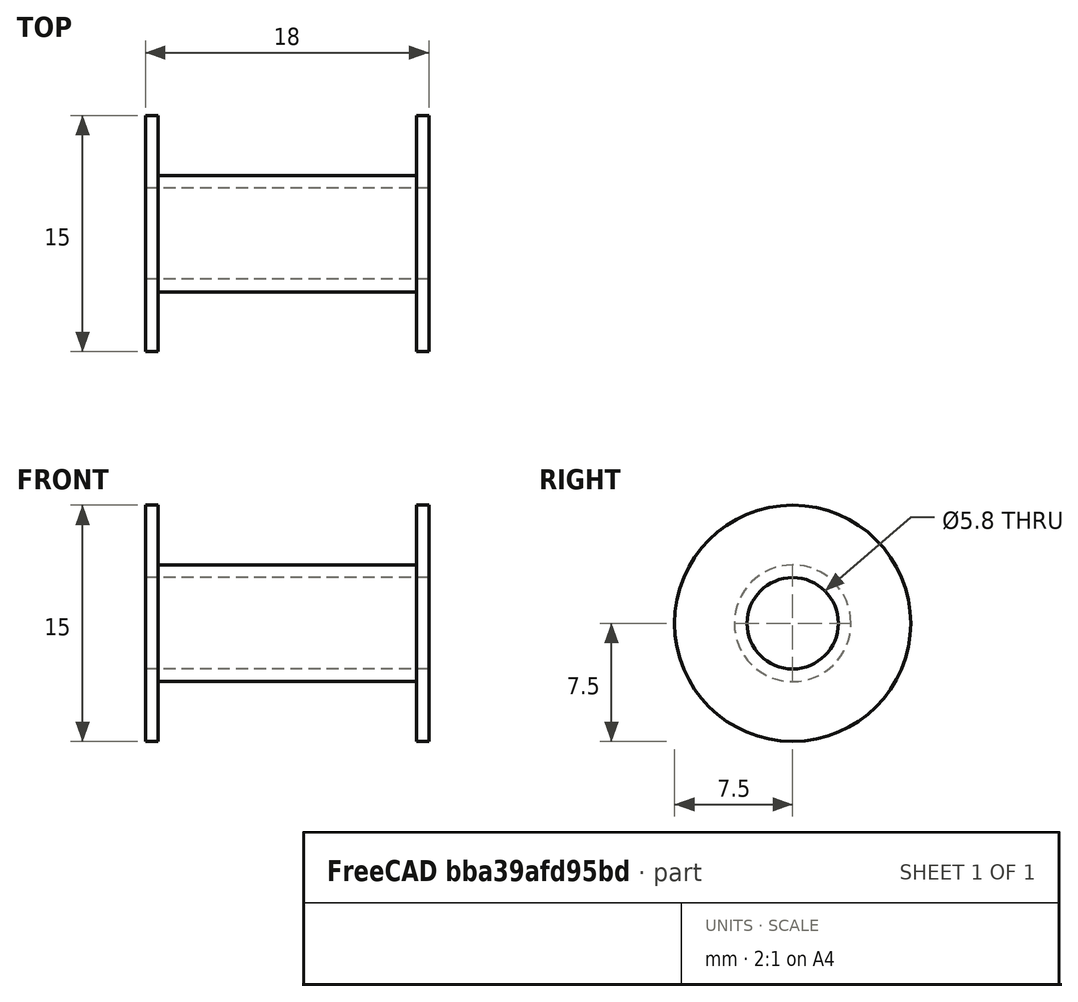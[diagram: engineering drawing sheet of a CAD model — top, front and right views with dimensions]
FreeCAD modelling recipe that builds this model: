
FCSTD DOCUMENT  (FreeCAD 0.17R13541 (Git))
Label: coil-core
License: All rights reserved
LicenseURL: http://en.wikipedia.org/wiki/All_rights_reserved
objects: Sketcher::SketchObject×1, PartDesign::Revolution×1, PartDesign::Body×1
note: 4 computed .brp shape members not serialized (recipe doc carries the construction recipe); baked Part::Feature solids carry a one-line shape summary decoded from their .brp

FEATURE [Sketcher::SketchObject] Sketch
  MapMode = 5
  Placement = pos=(0,0,0) rot=(1,0,0;1.5708rad)
  Support = -> [XZ_Plane]
  sketch-geometry (8):
    g0: LineSegment StartX=-9 StartY=-2.9 StartZ=0 EndX=-9 EndY=-7.5 EndZ=0
    g1: LineSegment StartX=-9 StartY=-7.5 StartZ=0 EndX=-8.2 EndY=-7.5 EndZ=0
    g2: LineSegment StartX=-8.2 StartY=-7.5 StartZ=0 EndX=-8.2 EndY=-3.7 EndZ=0
    g3: LineSegment StartX=-8.2 StartY=-3.7 StartZ=0 EndX=8.2 EndY=-3.7 EndZ=0
    g4: LineSegment StartX=8.2 StartY=-3.7 StartZ=0 EndX=8.2 EndY=-7.5 EndZ=0
    g5: LineSegment StartX=8.2 StartY=-7.5 StartZ=0 EndX=9 EndY=-7.5 EndZ=0
    g6: LineSegment StartX=9 StartY=-7.5 StartZ=0 EndX=9 EndY=-2.9 EndZ=0
    g7: LineSegment StartX=9 StartY=-2.9 StartZ=0 EndX=-9 EndY=-2.9 EndZ=0
  constraints (23):
    c: Vertical(g0)
    c: Horizontal(g1)
    c: Coincident(g1,g2)
    c: Vertical(g2)
    c: Coincident(g2,g3)
    c: Horizontal(g3)
    c: Coincident(g3,g4)
    c: Vertical(g4)
    c: Coincident(g4,g5)
    c: Coincident(g5,g6)
    c: Vertical(g6)
    c: Coincident(g7,g0)
    c: Horizontal(g5)
    c: Distance(g5) = 0.8
    c: Equal(g2,g4)
    c: Equal(g1,g5)
    c: Coincident(g0,g1)
    c: Symmetric(g0,g7,g-2)
    c: DistanceY(g0,g-1) = 2.9
    c: Coincident(g6,g7)
    c: DistanceY(g2,g0) = 0.8
    c: Distance(g0) = 4.6
    c: Distance(g0,g5) = 18
FEATURE [PartDesign::Revolution] Revolution
  Angle = 360
  Axis = (1,0,0)
  Base = (0,0,0)
  Placement = pos=(0,0,0) rot=(1,0,0;1.5708rad)
  Profile = -> Sketch
  ReferenceAxis = -> Sketch [H_Axis]
  Reversed = true
FEATURE [PartDesign::Body] Body
  Group = -> [Sketch,Revolution]
  Origin = -> Origin
  Tip = -> Revolution
